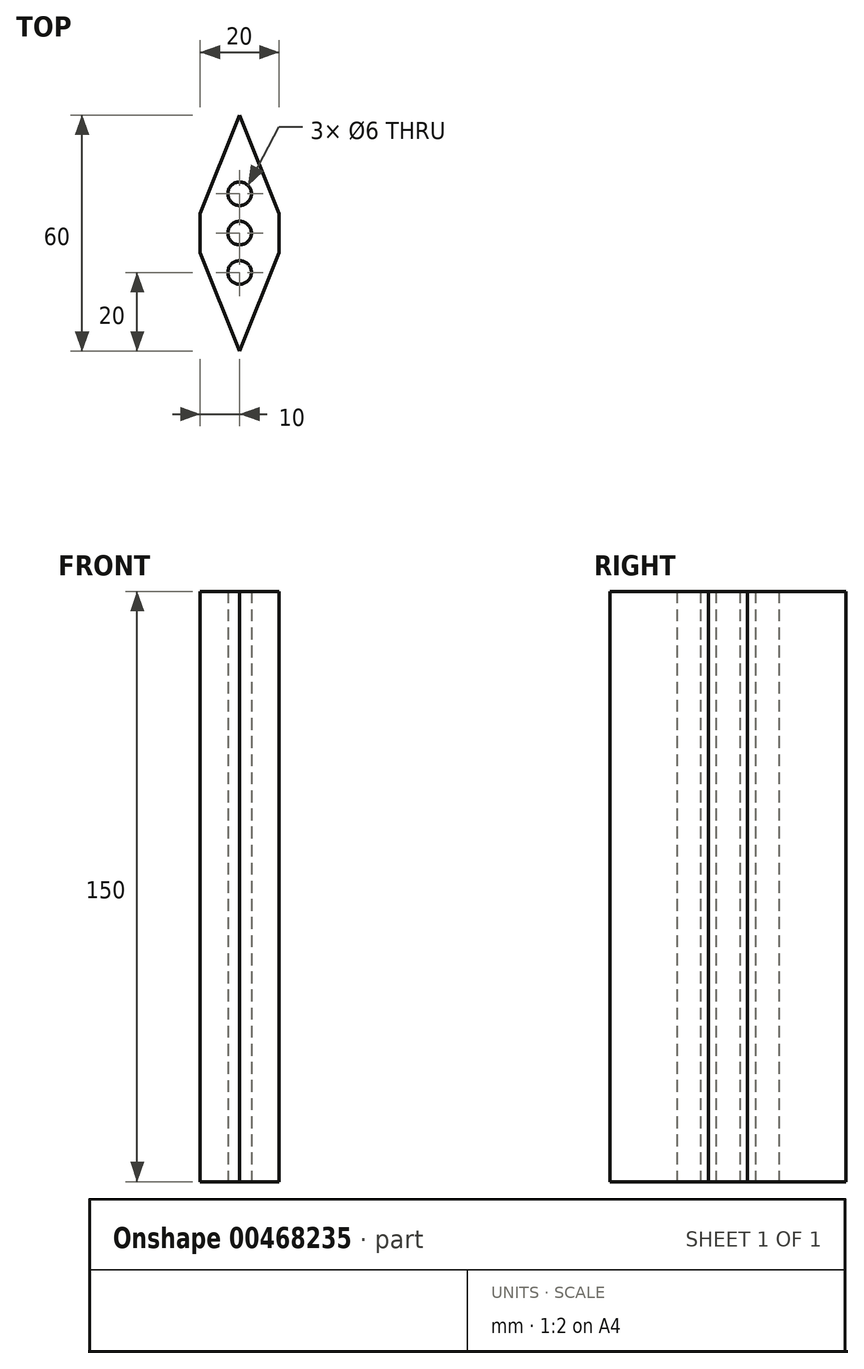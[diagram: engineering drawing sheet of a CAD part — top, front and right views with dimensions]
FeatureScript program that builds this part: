
annotation { "Feature Type Name" : "Feature", "Feature Type Description" : "" }
export const myFeature = defineFeature(function(context is Context, id is Id, definition is map)
    precondition{}
    {
        {
            var Q0;
            Q0=qCreatedBy(makeId("Top.planeOp"),FACE);
            var sketch = newSketch(context, id + "F0", { "sketchPlane" : qUnion([Q0])});
            skLineSegment(sketch, "E0.bottom", {"start": v(10, -30) * mm, "end": v(-10, -30) * mm});
            skLineSegment(sketch, "E0.top", {"start": v(10, 30) * mm, "end": v(-10, 30) * mm});
            skLineSegment(sketch, "E0.left", {"start": v(10, -30) * mm, "end": v(10, 30) * mm});
            skLineSegment(sketch, "E0.right", {"start": v(-10, -30) * mm, "end": v(-10, 30) * mm});
            skPoint(sketch, "E0.middle", {"position": v(0, 0) * mm});
            skLineSegment(sketch, "E1", {"start": v(0, 0) * mm, "end": v(0, 10) * mm});
            skLineSegment(sketch, "E2", {"start": v(0, 0) * mm, "end": v(0, -10) * mm});
            skSolve(sketch);
        }
        {
            var Q0;
            Q0=makeQuery(id+"F0.imprint","IMPRINT",FACE,{"disambiguationData":[TD([[makeQuery(id+"F0.imprint","IMPRINT",EDGE,{"derivedFrom":sQuery(id+"F0.wireOp",EDGE,"E0.bottom")}),-1.0]])]});
            extrude(context, id + "F1", {"entities" : qUnion([Q0]), "depth" : 150 * mm});
        }
        {
            var Q0;
            Q0=sQuery(id+"F0.wireOp",VERTEX,"E1.end");
            var Q1;
            Q1=sQuery(id+"F0.wireOp",VERTEX,"E0.middle");
            var Q2;
            Q2=sQuery(id+"F0.wireOp",VERTEX,"E2.end");
            var Q3;
            Q3=makeQuery(id+"F1.opExtrude","SWEPT_BODY",BODY,{"disambiguationData":[OSD([sQuery(id+"F0.wireOp",EDGE,"E0.bottom"),sQuery(id+"F0.wireOp",EDGE,"E0.top"),sQuery(id+"F0.wireOp",EDGE,"E0.left"),sQuery(id+"F0.wireOp",EDGE,"E0.right")])]});
            hole(context, id + "F2", {"style" : HoleStyle.SIMPLE, "endStyle" : HoleEndStyle.BLIND, "oppositeDirection" : true, "holeDiameter" : 6 * mm, "holeDepth" : 150 * mm, "isTappedThrough" : true, "tappedDepth" : 12 * mm, "tapClearance" : 3, "locations" : qUnion([Q0, Q1, Q2]), "scope" : qUnion([Q3])});
        }
        {
            var Q0;
            Q0=makeQuery(id+"F1.opExtrude","SWEPT_EDGE",EDGE,{"disambiguationData":[OSD([sQuery(id+"F0.wireOp",EDGE,"E0.top"),sQuery(id+"F0.wireOp",EDGE,"E0.right")])]});
            var Q1;
            Q1=makeQuery(id+"F1.opExtrude","SWEPT_EDGE",EDGE,{"disambiguationData":[OSD([sQuery(id+"F0.wireOp",EDGE,"E0.bottom"),sQuery(id+"F0.wireOp",EDGE,"E0.right")])]});
            var Q2;
            Q2=makeQuery(id+"F1.opExtrude","SWEPT_EDGE",EDGE,{"disambiguationData":[OSD([sQuery(id+"F0.wireOp",EDGE,"E0.bottom"),sQuery(id+"F0.wireOp",EDGE,"E0.left")])]});
            var Q3;
            Q3=makeQuery(id+"F1.opExtrude","SWEPT_EDGE",EDGE,{"disambiguationData":[OSD([sQuery(id+"F0.wireOp",EDGE,"E0.top"),sQuery(id+"F0.wireOp",EDGE,"E0.left")])]});
            chamfer(context, id + "F3", {"entities" : qUnion([Q0, Q1, Q2, Q3]), "chamferType" : ChamferType.TWO_OFFSETS, "width1" : 25 * mm, "oppositeDirection" : false, "width2" : 10 * mm, "tangentPropagation" : true});
        }
    });
